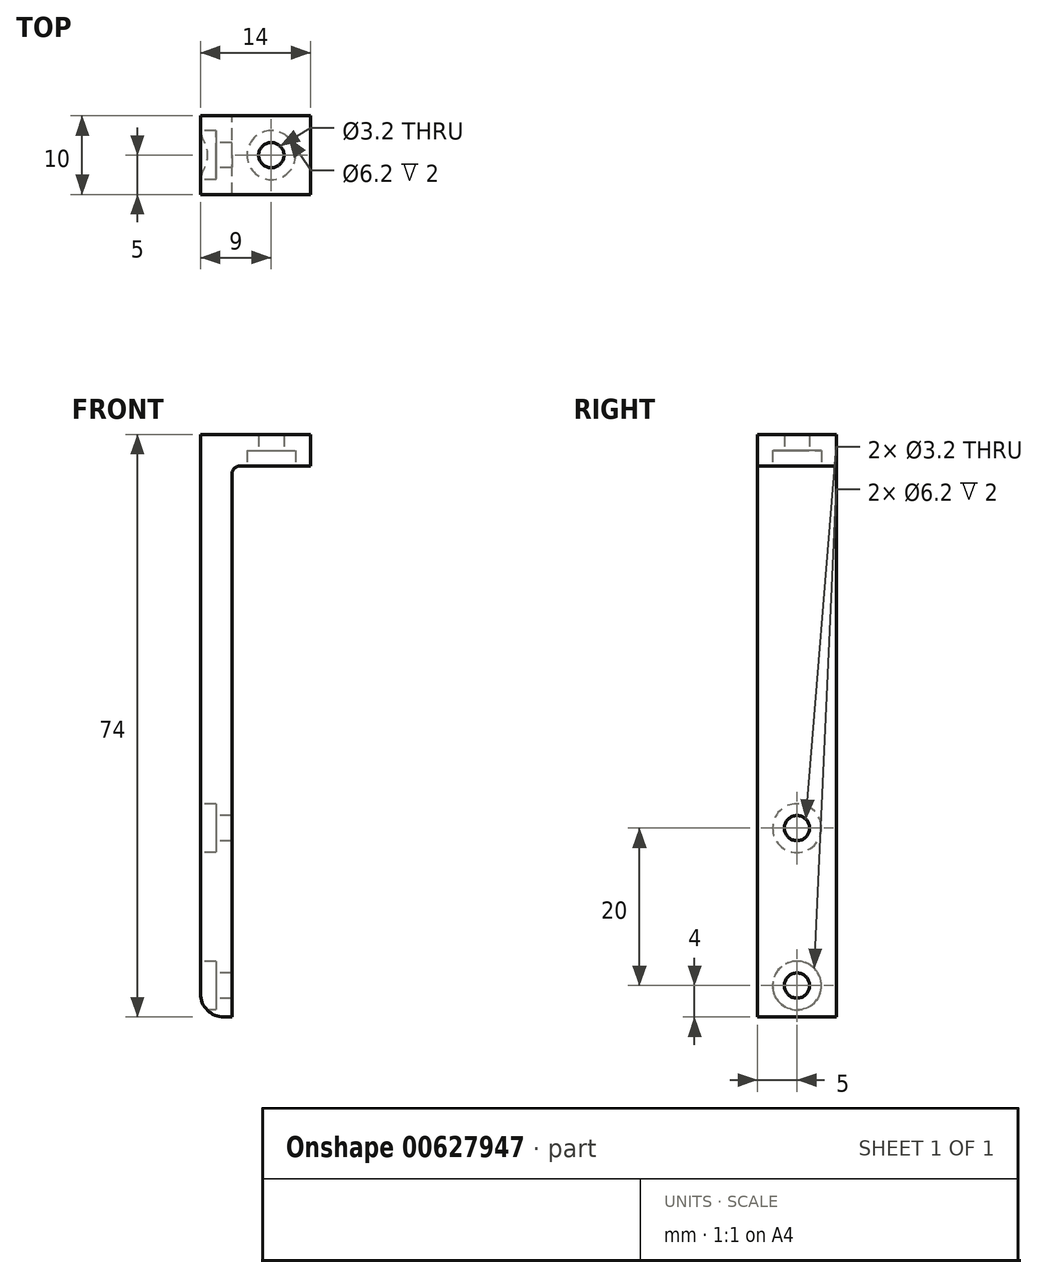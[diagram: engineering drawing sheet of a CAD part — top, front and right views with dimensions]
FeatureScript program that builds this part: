
annotation { "Feature Type Name" : "Feature", "Feature Type Description" : "" }
export const myFeature = defineFeature(function(context is Context, id is Id, definition is map)
    precondition{}
    {
        {
            var Q0;
            Q0=qCreatedBy(makeId("Front.planeOp"),FACE);
            var sketch = newSketch(context, id + "F0", { "sketchPlane" : qUnion([Q0])});
            skLineSegment(sketch, "E0", {"start": v(0, 0) * mm, "end": v(0, 74) * mm});
            skLineSegment(sketch, "E1", {"start": v(0, 74) * mm, "end": v(14, 74) * mm});
            skLineSegment(sketch, "E2", {"start": v(14, 74) * mm, "end": v(14, 70) * mm});
            skLineSegment(sketch, "E3", {"start": v(14, 70) * mm, "end": v(4, 70) * mm});
            skLineSegment(sketch, "E4", {"start": v(4, 70) * mm, "end": v(4, 0) * mm});
            skLineSegment(sketch, "E5", {"start": v(4, 0) * mm, "end": v(0, 0) * mm});
            skSolve(sketch);
        }
        {
            var Q0;
            Q0=makeQuery(id+"F0.imprint","IMPRINT",FACE,{"disambiguationData":[TD([[makeQuery(id+"F0.imprint","IMPRINT",EDGE,{"derivedFrom":sQuery(id+"F0.wireOp",EDGE,"E0")}),-1.0]])]});
            extrude(context, id + "F1", {"entities" : qUnion([Q0]), "endBound" : BoundingType.SYMMETRIC, "depth" : 10 * mm, "offsetDistance" : 25 * mm});
        }
        {
            var Q0;
            Q0=makeQuery(id+"F1.opExtrude","SWEPT_FACE",FACE,{"disambiguationData":[OSD([sQuery(id+"F0.wireOp",EDGE,"E0")])]});
            var sketch = newSketch(context, id + "F2", { "sketchPlane" : qUnion([Q0])});
            skPoint(sketch, "E6", {"position": v(0, 4) * mm});
            skPoint(sketch, "E7", {"position": v(0, 24) * mm});
            skLineSegment(sketch, "E8", {"start": v(-5, 28) * mm, "end": v(5, 28) * mm, "construction": true});
            skSolve(sketch);
        }
        {
            var Q0;
            Q0=makeQuery(id+"F1.opExtrude","SWEPT_FACE",FACE,{"disambiguationData":[OSD([sQuery(id+"F0.wireOp",EDGE,"E3")])]});
            var sketch = newSketch(context, id + "F3", { "sketchPlane" : qUnion([Q0])});
            skPoint(sketch, "E9", {"position": v(9, 0) * mm});
            skSolve(sketch);
        }
        {
            var Q0;
            Q0=sQuery(id+"F2.wireOp",VERTEX,"E7");
            var Q1;
            Q1=sQuery(id+"F2.wireOp",VERTEX,"E6");
            var Q2;
            Q2=sQuery(id+"F3.wireOp",VERTEX,"E9");
            var Q3;
            Q3=makeQuery(id+"F1.opExtrude","SWEPT_BODY",BODY,{"disambiguationData":[OSD([sQuery(id+"F0.wireOp",EDGE,"E0"),sQuery(id+"F0.wireOp",EDGE,"E1"),sQuery(id+"F0.wireOp",EDGE,"E2"),sQuery(id+"F0.wireOp",EDGE,"E3"),sQuery(id+"F0.wireOp",EDGE,"E4"),sQuery(id+"F0.wireOp",EDGE,"E5")])]});
            hole(context, id + "F4", {"style" : HoleStyle.C_BORE, "endStyle" : HoleEndStyle.THROUGH, "holeDiameter" : 3.2 * mm, "cBoreDiameter" : 6.2 * mm, "cBoreDepth" : 2 * mm, "majorDiameter" : 5 * mm, "isTappedThrough" : true, "tappedDepth" : 2.3 * mm, "tapClearance" : 3, "startFromSketch" : true, "locations" : qUnion([Q0, Q1, Q2]), "scope" : qUnion([Q3])});
        }
        {
            var Q0;
            Q0=makeQuery(id+"F1.opExtrude","SWEPT_EDGE",EDGE,{"disambiguationData":[OSD([sQuery(id+"F0.wireOp",EDGE,"E3"),sQuery(id+"F0.wireOp",EDGE,"E4")])]});
            fillet(context, id + "F5", {"entities" : qUnion([Q0]), "radius" : 1 * mm, "tangentPropagation" : true, "allowEdgeOverflow" : false});
        }
        {
            var Q0;
            Q0=makeQuery(id+"F1.opExtrude","SWEPT_EDGE",EDGE,{"disambiguationData":[OSD([sQuery(id+"F0.wireOp",EDGE,"E0"),sQuery(id+"F0.wireOp",EDGE,"E5")])]});
            fillet(context, id + "F6", {"entities" : qUnion([Q0]), "radius" : 3 * mm, "tangentPropagation" : true, "allowEdgeOverflow" : false});
        }
    });
